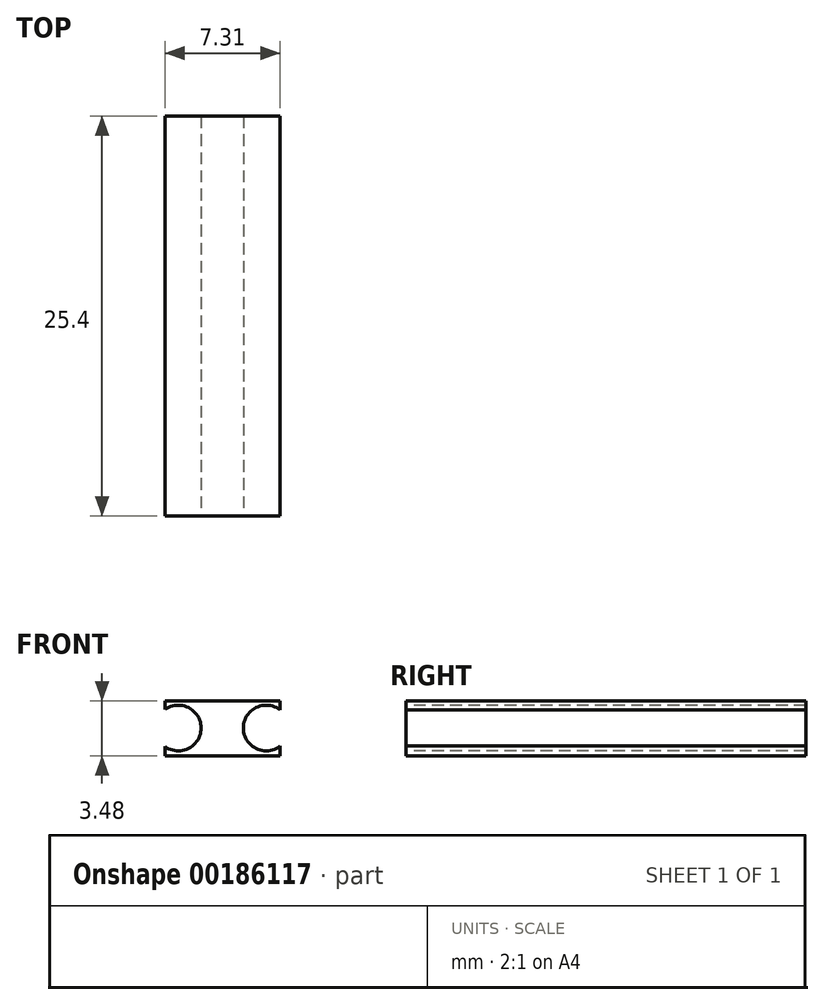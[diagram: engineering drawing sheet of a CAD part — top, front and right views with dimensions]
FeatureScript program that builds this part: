
annotation { "Feature Type Name" : "Feature", "Feature Type Description" : "" }
export const myFeature = defineFeature(function(context is Context, id is Id, definition is map)
    precondition{}
    {
        {
            var Q0;
            Q0=qCreatedBy(makeId("Front.planeOp"),FACE);
            var sketch = newSketch(context, id + "F0", { "sketchPlane" : qUnion([Q0])});
            skLineSegment(sketch, "E0.bottom", {"start": v(-30.72, 14.6) * mm, "end": v(-23.41, 14.6) * mm});
            skLineSegment(sketch, "E0.top", {"start": v(-30.72, 18.08) * mm, "end": v(-23.41, 18.08) * mm});
            skLineSegment(sketch, "E0.left", {"start": v(-30.72, 14.6) * mm, "end": v(-30.72, 18.08) * mm});
            skLineSegment(sketch, "E0.right", {"start": v(-23.41, 14.6) * mm, "end": v(-23.41, 18.08) * mm});
            skSolve(sketch);
        }
        {
            var Q0;
            Q0=makeQuery(id+"F0.imprint","IMPRINT",FACE,{"disambiguationData":[TD([[makeQuery(id+"F0.imprint","IMPRINT",EDGE,{"derivedFrom":sQuery(id+"F0.wireOp",EDGE,"E0.bottom")}),1.0]])]});
            extrude(context, id + "F1", {"entities" : qUnion([Q0]), "depth" : 25.4 * mm});
        }
        {
            var Q0;
            Q0=makeQuery(id+"F1.opExtrude","CAP_FACE",FACE,{"disambiguationData":[OSD([sQuery(id+"F0.wireOp",EDGE,"E0.bottom"),sQuery(id+"F0.wireOp",EDGE,"E0.top"),sQuery(id+"F0.wireOp",EDGE,"E0.left"),sQuery(id+"F0.wireOp",EDGE,"E0.right")])],"isStart":false});
            var sketch = newSketch(context, id + "F2", { "sketchPlane" : qUnion([Q0])});
            skCircle(sketch, "E1", {"center": v(-29.87, 16.36) * mm, "radius": 1.45 * mm});
            skSolve(sketch);
        }
        {
            var Q0;
            Q0=sQuery(id+"F2.wireOp",VERTEX,"E1.center");
            var Q1;
            Q1=makeQuery(id+"F1.opExtrude","SWEPT_BODY",BODY,{"disambiguationData":[OSD([sQuery(id+"F0.wireOp",EDGE,"E0.bottom"),sQuery(id+"F0.wireOp",EDGE,"E0.top"),sQuery(id+"F0.wireOp",EDGE,"E0.left"),sQuery(id+"F0.wireOp",EDGE,"E0.right")])]});
            hole(context, id + "F3", {"style" : HoleStyle.SIMPLE, "endStyle" : HoleEndStyle.THROUGH, "holeDiameter" : 2.9 * mm, "locations" : qUnion([Q0]), "scope" : qUnion([Q1]), "isTappedThrough" : true});
        }
        {
            var Q0;
            Q0=makeQuery(id+"F1.opExtrude","CAP_FACE",FACE,{"disambiguationData":[OSD([sQuery(id+"F0.wireOp",EDGE,"E0.bottom"),sQuery(id+"F0.wireOp",EDGE,"E0.top"),sQuery(id+"F0.wireOp",EDGE,"E0.left"),sQuery(id+"F0.wireOp",EDGE,"E0.right")])],"isStart":false});
            var sketch = newSketch(context, id + "F4", { "sketchPlane" : qUnion([Q0])});
            skCircle(sketch, "E2", {"center": v(-24.3, 16.36) * mm, "radius": 1.46 * mm});
            skSolve(sketch);
        }
        {
            var Q0;
            Q0=sQuery(id+"F4.wireOp",VERTEX,"E2.center");
            var Q1;
            Q1=makeQuery(id+"F1.opExtrude","SWEPT_BODY",BODY,{"disambiguationData":[OSD([sQuery(id+"F0.wireOp",EDGE,"E0.bottom"),sQuery(id+"F0.wireOp",EDGE,"E0.top"),sQuery(id+"F0.wireOp",EDGE,"E0.left"),sQuery(id+"F0.wireOp",EDGE,"E0.right")])]});
            hole(context, id + "F5", {"style" : HoleStyle.SIMPLE, "endStyle" : HoleEndStyle.THROUGH, "holeDiameter" : 2.9 * mm, "locations" : qUnion([Q0]), "scope" : qUnion([Q1]), "isTappedThrough" : true});
        }
    });
